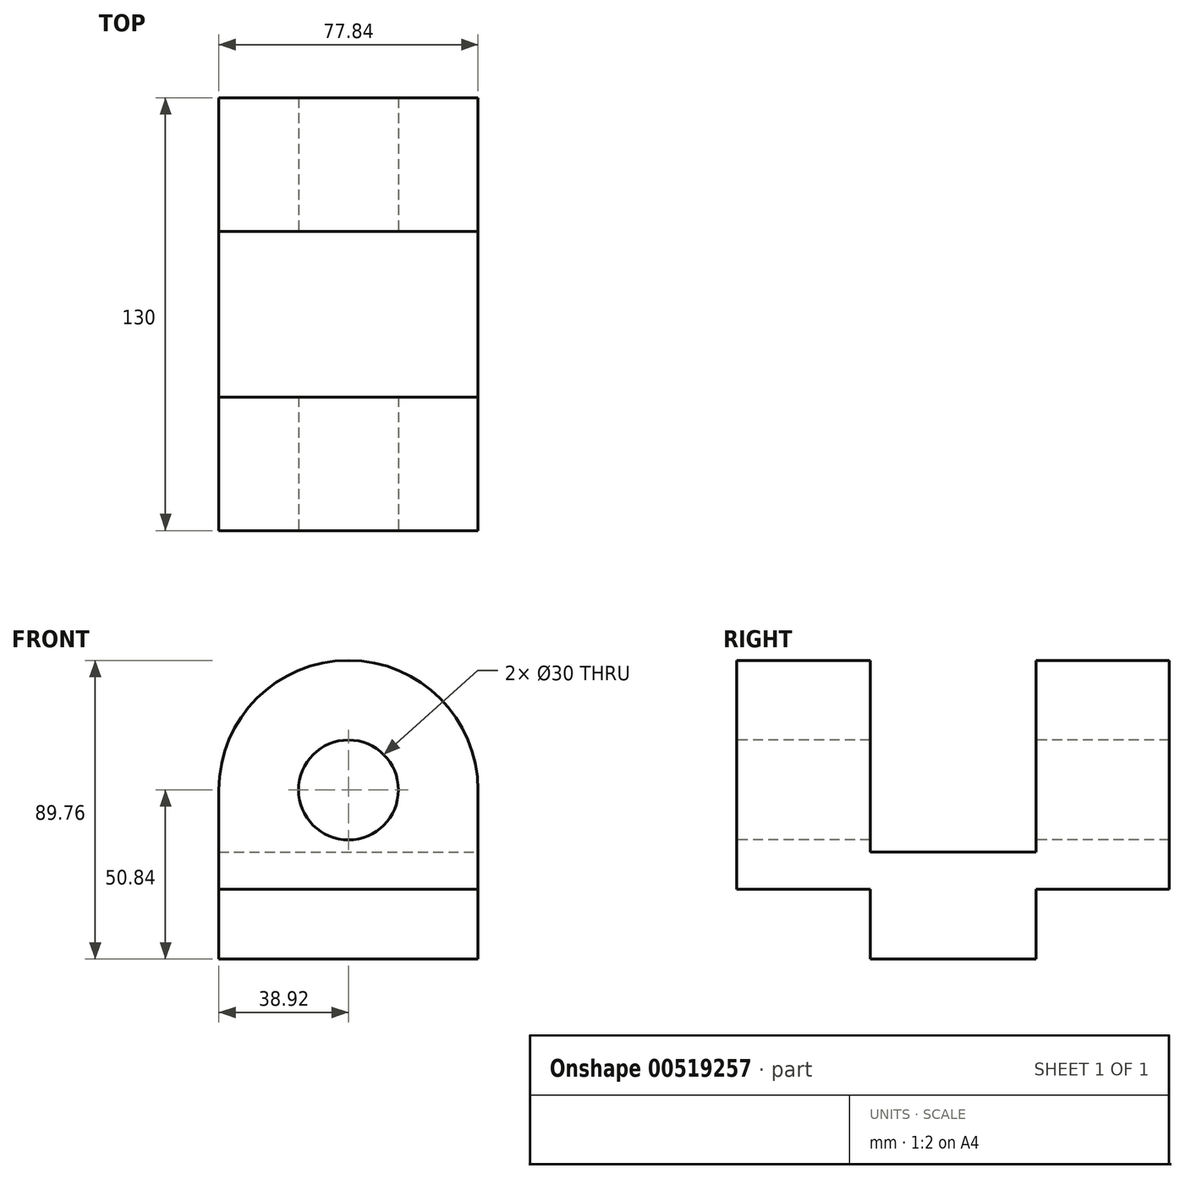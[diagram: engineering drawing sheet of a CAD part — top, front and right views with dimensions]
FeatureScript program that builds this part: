
annotation { "Feature Type Name" : "Feature", "Feature Type Description" : "" }
export const myFeature = defineFeature(function(context is Context, id is Id, definition is map)
    precondition{}
    {
        {
            var Q0;
            Q0=qCreatedBy(makeId("Front.planeOp"),FACE);
            var sketch = newSketch(context, id + "F0", { "sketchPlane" : qUnion([Q0])});
            skArc(sketch, "E0", {"start": v(38.92, 0) * mm, "mid": v(0, 38.92) * mm, "end": v(-38.92, 0) * mm});
            skLineSegment(sketch, "E1.top", {"start": v(-38.92, -50.84) * mm, "end": v(38.92, -50.84) * mm});
            skLineSegment(sketch, "E1.left", {"start": v(-38.92, 0) * mm, "end": v(-38.92, -50.84) * mm});
            skLineSegment(sketch, "E1.right", {"start": v(38.92, 0) * mm, "end": v(38.92, -50.84) * mm});
            skSolve(sketch);
        }
        {
            var Q0;
            Q0=makeQuery(id+"F0.imprint","IMPRINT",FACE,{"disambiguationData":[TD([[makeQuery(id+"F0.imprint","IMPRINT",EDGE,{"derivedFrom":sQuery(id+"F0.wireOp",EDGE,"E0")}),1.0]])]});
            extrude(context, id + "F1", {"entities" : qUnion([Q0]), "endBound" : BoundingType.SYMMETRIC, "depth" : 130 * mm, "offsetDistance" : 25 * mm});
        }
        {
            var Q0;
            Q0=makeQuery(id+"F1.opExtrude","CAP_FACE",FACE,{"disambiguationData":[OSD([sQuery(id+"F0.wireOp",EDGE,"E0"),sQuery(id+"F0.wireOp",EDGE,"E1.top"),sQuery(id+"F0.wireOp",EDGE,"E1.left"),sQuery(id+"F0.wireOp",EDGE,"E1.right")])],"isStart":false});
            var sketch = newSketch(context, id + "F2", { "sketchPlane" : qUnion([Q0])});
            skLineSegment(sketch, "E2.bottom", {"start": v(38.92, -50.84) * mm, "end": v(-38.92, -50.84) * mm});
            skLineSegment(sketch, "E2.top", {"start": v(38.92, -25.42) * mm, "end": v(-38.92, -25.42) * mm});
            skLineSegment(sketch, "E2.left", {"start": v(38.92, -50.84) * mm, "end": v(38.92, -25.42) * mm});
            skLineSegment(sketch, "E2.right", {"start": v(-38.92, -50.84) * mm, "end": v(-38.92, -25.42) * mm});
            skSolve(sketch);
        }
        {
            var Q0;
            Q0=makeQuery(id+"F1.opExtrude","SWEPT_FACE",FACE,{"disambiguationData":[OSD([sQuery(id+"F0.wireOp",EDGE,"E1.right")])]});
            var sketch = newSketch(context, id + "F3", { "sketchPlane" : qUnion([Q0])});
            skLineSegment(sketch, "E3.bottom", {"start": v(-65, -50.84) * mm, "end": v(-24.88, -50.84) * mm});
            skLineSegment(sketch, "E3.top", {"start": v(-65, -29.86) * mm, "end": v(-24.88, -29.86) * mm});
            skLineSegment(sketch, "E3.left", {"start": v(-65, -50.84) * mm, "end": v(-65, -29.86) * mm});
            skLineSegment(sketch, "E3.right", {"start": v(-24.88, -50.84) * mm, "end": v(-24.88, -29.86) * mm});
            skLineSegment(sketch, "E4.bottom", {"start": v(65, -50.84) * mm, "end": v(24.88, -50.84) * mm});
            skLineSegment(sketch, "E4.top", {"start": v(65, -29.86) * mm, "end": v(24.88, -29.86) * mm});
            skLineSegment(sketch, "E4.left", {"start": v(65, -50.84) * mm, "end": v(65, -29.86) * mm});
            skLineSegment(sketch, "E4.right", {"start": v(24.88, -50.84) * mm, "end": v(24.88, -29.86) * mm});
            skLineSegment(sketch, "E5", {"start": v(0, -50.84) * mm, "end": v(0, 38.49) * mm, "construction": true});
            skPoint(sketch, "E5.endSnap0", {"position": v(0, -50.84) * mm});
            skLineSegment(sketch, "E6", {"start": v(-65, 38.92) * mm, "end": v(65, 38.92) * mm, "construction": true});
            skLineSegment(sketch, "E7.bottom", {"start": v(-24.88, 38.92) * mm, "end": v(24.88, 38.92) * mm});
            skLineSegment(sketch, "E7.top", {"start": v(-24.88, -18.61) * mm, "end": v(24.88, -18.61) * mm});
            skLineSegment(sketch, "E7.left", {"start": v(-24.88, 38.92) * mm, "end": v(-24.88, -18.61) * mm});
            skLineSegment(sketch, "E7.right", {"start": v(24.88, 38.92) * mm, "end": v(24.88, -18.61) * mm});
            skSolve(sketch);
        }
        {
            var Q0;
            Q0=makeQuery(id+"F3.imprint","IMPRINT",FACE,{"disambiguationData":[TD([[makeQuery(id+"F3.imprint","IMPRINT",EDGE,{"derivedFrom":sQuery(id+"F3.wireOp",EDGE,"E3.bottom")}),1.0]])]});
            var Q1;
            Q1=makeQuery(id+"F3.imprint","IMPRINT",FACE,{"disambiguationData":[TD([[makeQuery(id+"F3.imprint","IMPRINT",EDGE,{"derivedFrom":sQuery(id+"F3.wireOp",EDGE,"E4.bottom")}),1.0]])]});
            var Q2;
            {var subQ0=sQuery(id+"F3.wireOp",EDGE,"E7.bottom");Q2=makeQuery(id+"F3.imprint","IMPRINT",FACE,{"disambiguationData":[TD([[makeQuery(id+"F3.imprint","IMPRINT",EDGE,{"derivedFrom":subQ0}),-1.0]])]});}
            var Q3;
            {var subQ0=sQuery(id+"F3.wireOp",EDGE,"E7.top");Q3=makeQuery(id+"F3.imprint","IMPRINT",FACE,{"disambiguationData":[TD([[makeQuery(id+"F3.imprint","IMPRINT",EDGE,{"derivedFrom":subQ0}),1.0]])]});}
            extrude(context, id + "F4", {"entities" : qUnion([Q0, Q1, Q2, Q3]), "operationType" : NewBodyOperationType.REMOVE, "endBound" : BoundingType.THROUGH_ALL, "oppositeDirection" : true, "depth" : 25 * mm, "offsetDistance" : 25 * mm});
        }
        {
            var Q0;
            {var subQ0=sQuery(id+"F2.wireOp",EDGE,"E2.top");Q0=makeQuery(id+"F2.imprint","IMPRINT",FACE,{"disambiguationData":[TD([[makeQuery(id+"F2.imprint","IMPRINT",EDGE,{"derivedFrom":subQ0}),-1.0]])]});}
            var sketch = newSketch(context, id + "F5", { "sketchPlane" : qUnion([Q0])});
            skCircle(sketch, "E8", {"center": v(0, 0) * mm, "radius": 15 * mm});
            skSolve(sketch);
        }
        {
            var Q0;
            Q0=makeQuery(id+"F5.imprint","IMPRINT",FACE,{"disambiguationData":[TD([[makeQuery(id+"F5.imprint","IMPRINT",EDGE,{"derivedFrom":sQuery(id+"F5.wireOp",EDGE,"E8")}),1.0]])]});
            extrude(context, id + "F6", {"entities" : qUnion([Q0]), "operationType" : NewBodyOperationType.REMOVE, "endBound" : BoundingType.THROUGH_ALL, "oppositeDirection" : true, "depth" : 25 * mm, "offsetDistance" : 25 * mm});
        }
    });
